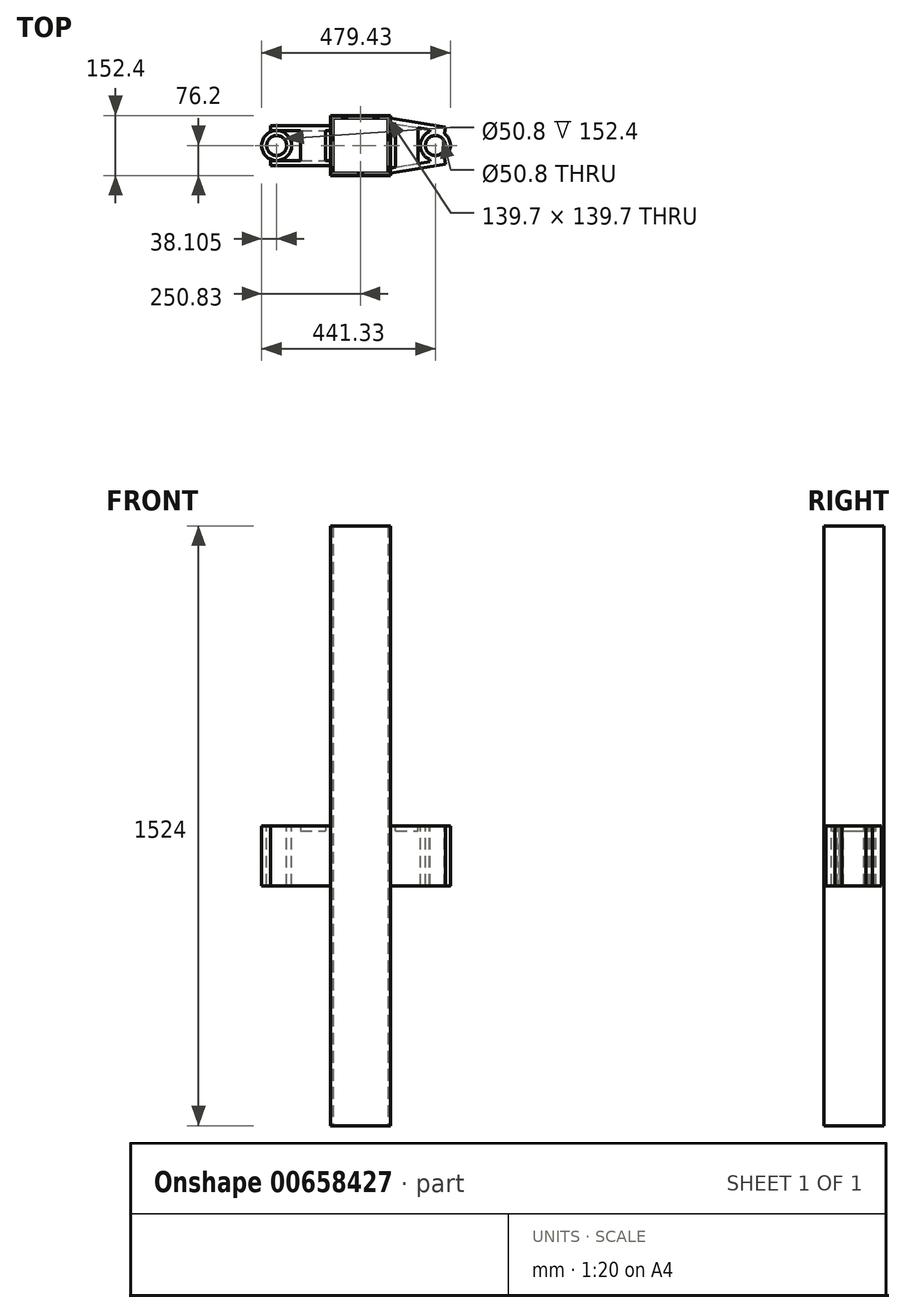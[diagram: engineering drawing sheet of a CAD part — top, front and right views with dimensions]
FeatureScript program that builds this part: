
annotation { "Feature Type Name" : "Feature", "Feature Type Description" : "" }
export const myFeature = defineFeature(function(context is Context, id is Id, definition is map)
    precondition{}
    {
        {
            var Q0;
            Q0=qCreatedBy(makeId("Top.planeOp"),FACE);
            var sketch = newSketch(context, id + "F0", { "sketchPlane" : qUnion([Q0])});
            skLineSegment(sketch, "E0.bottom", {"start": v(-76.2, -76.2) * mm, "end": v(76.2, -76.2) * mm});
            skLineSegment(sketch, "E0.top", {"start": v(-76.2, 76.2) * mm, "end": v(76.2, 76.2) * mm});
            skLineSegment(sketch, "E0.left", {"start": v(-76.2, -76.2) * mm, "end": v(-76.2, 76.2) * mm});
            skLineSegment(sketch, "E0.right", {"start": v(76.2, -76.2) * mm, "end": v(76.2, 76.2) * mm});
            skLineSegment(sketch, "E1.0", {"start": v(-69.85, 69.85) * mm, "end": v(69.85, 69.85) * mm});
            skLineSegment(sketch, "E1.1", {"start": v(-69.85, -69.85) * mm, "end": v(-69.85, 69.85) * mm});
            skLineSegment(sketch, "E1.2", {"start": v(-69.85, -69.85) * mm, "end": v(69.85, -69.85) * mm});
            skLineSegment(sketch, "E1.3", {"start": v(69.85, -69.85) * mm, "end": v(69.85, 69.85) * mm});
            skSolve(sketch);
        }
        {
            var Q0;
            Q0=makeQuery(id+"F0.imprint","IMPRINT",FACE,{"disambiguationData":[TD([[makeQuery(id+"F0.imprint","IMPRINT",EDGE,{"derivedFrom":sQuery(id+"F0.wireOp",EDGE,"E0.bottom")}),1.0]])]});
            extrude(context, id + "F1", {"entities" : qUnion([Q0]), "depth" : 1524 * mm, "offsetDistance" : 25.4 * mm});
        }
        {
            var Q0;
            Q0=makeQuery(id+"F1.opExtrude","SWEPT_FACE",FACE,{"disambiguationData":[OSD([sQuery(id+"F0.wireOp",EDGE,"E0.left")])]});
            var sketch = newSketch(context, id + "F2", { "sketchPlane" : qUnion([Q0])});
            skLineSegment(sketch, "E2.bottom", {"start": v(-50.8, 609.6) * mm, "end": v(-38.1, 609.6) * mm});
            skLineSegment(sketch, "E2.top", {"start": v(-50.8, 762) * mm, "end": v(-38.1, 762) * mm});
            skLineSegment(sketch, "E2.left", {"start": v(-50.8, 609.6) * mm, "end": v(-50.8, 762) * mm});
            skLineSegment(sketch, "E2.right", {"start": v(-38.1, 609.6) * mm, "end": v(-38.1, 762) * mm});
            skLineSegment(sketch, "E3.bottom", {"start": v(38.1, 762) * mm, "end": v(50.8, 762) * mm});
            skLineSegment(sketch, "E3.top", {"start": v(38.1, 609.6) * mm, "end": v(50.8, 609.6) * mm});
            skLineSegment(sketch, "E3.left", {"start": v(38.1, 762) * mm, "end": v(38.1, 609.6) * mm});
            skLineSegment(sketch, "E3.right", {"start": v(50.8, 762) * mm, "end": v(50.8, 609.6) * mm});
            skSolve(sketch);
        }
        {
            var Q0;
            Q0=makeQuery(id+"F2.imprint","IMPRINT",FACE,{"disambiguationData":[TD([[makeQuery(id+"F2.imprint","IMPRINT",EDGE,{"derivedFrom":sQuery(id+"F2.wireOp",EDGE,"E2.bottom")}),1.0]])]});
            var Q1;
            Q1=makeQuery(id+"F2.imprint","IMPRINT",FACE,{"disambiguationData":[TD([[makeQuery(id+"F2.imprint","IMPRINT",EDGE,{"derivedFrom":sQuery(id+"F2.wireOp",EDGE,"E3.bottom")}),-1.0]])]});
            extrude(context, id + "F3", {"entities" : qUnion([Q0, Q1]), "operationType" : NewBodyOperationType.ADD, "depth" : 152.4 * mm, "offsetDistance" : 25.4 * mm});
        }
        {
            var Q0;
            Q0=makeQuery(id+"F3.opExtrude","SWEPT_FACE",FACE,{"disambiguationData":[OSD([sQuery(id+"F2.wireOp",EDGE,"E2.top")])]});
            var sketch = newSketch(context, id + "F4", { "sketchPlane" : qUnion([Q0])});
            skCircle(sketch, "E4", {"center": v(-212.72, 0) * mm, "radius": 38.1 * mm});
            skCircle(sketch, "E5.0", {"center": v(-212.72, 0) * mm, "radius": 25.4 * mm});
            skSolve(sketch);
        }
        {
            var Q0;
            Q0=makeQuery(id+"F4.imprint","IMPRINT",FACE,{"disambiguationData":[TD([[makeQuery(id+"F4.imprint","IMPRINT",EDGE,{"derivedFrom":sQuery(id+"F4.wireOp",EDGE,"E4")}),1.0]])]});
            extrude(context, id + "F5", {"entities" : qUnion([Q0]), "operationType" : NewBodyOperationType.ADD, "oppositeDirection" : true, "depth" : 152.4 * mm, "offsetDistance" : 25.4 * mm});
        }
        {
            var Q0;
            Q0=makeQuery(id+"F3.opExtrude","SWEPT_FACE",FACE,{"disambiguationData":[OSD([sQuery(id+"F2.wireOp",EDGE,"E2.right")])]});
            var sketch = newSketch(context, id + "F6", { "sketchPlane" : qUnion([Q0])});
            skLineSegment(sketch, "E6.bottom", {"start": v(-152.4, 762) * mm, "end": v(-88.9, 762) * mm});
            skLineSegment(sketch, "E6.top", {"start": v(-152.4, 749.3) * mm, "end": v(-88.9, 749.3) * mm});
            skLineSegment(sketch, "E6.left", {"start": v(-152.4, 762) * mm, "end": v(-152.4, 749.3) * mm});
            skLineSegment(sketch, "E6.right", {"start": v(-88.9, 762) * mm, "end": v(-88.9, 749.3) * mm});
            skSolve(sketch);
        }
        {
            var Q0;
            Q0=makeQuery(id+"F6.imprint","IMPRINT",FACE,{"disambiguationData":[TD([[makeQuery(id+"F6.imprint","IMPRINT",EDGE,{"derivedFrom":sQuery(id+"F6.wireOp",EDGE,"E6.bottom")}),-1.0]])]});
            extrude(context, id + "F7", {"entities" : qUnion([Q0]), "operationType" : NewBodyOperationType.ADD, "endBound" : BoundingType.UP_TO_NEXT, "depth" : 25.4 * mm, "offsetDistance" : 25.4 * mm});
        }
        {
            var Q0;
            Q0=makeQuery(id+"F7.boolean.opBoolean","MERGE",FACE,{"derivedFrom":[makeQuery(id+"F3.opExtrude","SWEPT_FACE",FACE,{"disambiguationData":[OSD([sQuery(id+"F2.wireOp",EDGE,"E2.top")])]}),makeQuery(id+"F3.opExtrude","SWEPT_FACE",FACE,{"disambiguationData":[OSD([sQuery(id+"F2.wireOp",EDGE,"E3.bottom")])]}),makeQuery(id+"F7.opExtrude","SWEPT_FACE",FACE,{"disambiguationData":[OSD([sQuery(id+"F6.wireOp",EDGE,"E6.bottom")])]})]});
            var sketch = newSketch(context, id + "F8", { "sketchPlane" : qUnion([Q0])});
            skLineSegment(sketch, "E7.0", {"start": v(76.2, -76.2) * mm, "end": v(76.2, 76.2) * mm});
            skLineSegment(sketch, "E8.bottom", {"start": v(76.2, -76.2) * mm, "end": v(228.6, -76.2) * mm});
            skLineSegment(sketch, "E8.top", {"start": v(76.2, 76.2) * mm, "end": v(228.6, 76.2) * mm});
            skLineSegment(sketch, "E8.right", {"start": v(228.6, -76.2) * mm, "end": v(228.6, 76.2) * mm});
            skPoint(sketch, "E9", {"position": v(-228.6, 50.8) * mm});
            skPoint(sketch, "E10", {"position": v(-76.2, 50.8) * mm});
            skPoint(sketch, "E11", {"position": v(-228.6, 38.1) * mm});
            skPoint(sketch, "E12", {"position": v(-228.6, -38.1) * mm});
            skCircle(sketch, "E13", {"center": v(190.5, 0) * mm, "radius": 38.1 * mm});
            skPoint(sketch, "E13.centerSnap0", {"position": v(228.6, 0) * mm});
            skCircle(sketch, "E14", {"center": v(190.5, 0) * mm, "radius": 25.4 * mm});
            skLineSegment(sketch, "E15", {"start": v(76.2, 57.05) * mm, "end": v(214.11, 34.78) * mm});
            skLineSegment(sketch, "E16", {"start": v(76.2, -57.05) * mm, "end": v(214.11, -34.78) * mm});
            skLineSegment(sketch, "E17.0", {"start": v(76.2, 69.92) * mm, "end": v(216.14, 47.32) * mm});
            skLineSegment(sketch, "E18.0", {"start": v(76.2, -69.92) * mm, "end": v(216.14, -47.32) * mm});
            skLineSegment(sketch, "E19", {"start": v(216.14, 47.32) * mm, "end": v(213.41, 30.44) * mm});
            skLineSegment(sketch, "E20", {"start": v(216.14, -47.32) * mm, "end": v(213.41, -30.44) * mm});
            skLineSegment(sketch, "E21", {"start": v(176.5, -40.85) * mm, "end": v(175.56, -35.05) * mm});
            skLineSegment(sketch, "E22", {"start": v(176.5, 40.85) * mm, "end": v(175.56, 35.05) * mm});
            skSolve(sketch);
        }
        {
            var Q0;
            {var subQ7=sQuery(id+"F8.wireOp",EDGE,"E17.0");Q0=makeQuery(id+"F8.imprint","IMPRINT",FACE,{"disambiguationData":[TD([[makeQuery(id+"F8.imprint","IMPRINT",EDGE,{"derivedFrom":subQ7}),-1.0]])]});}
            var Q1;
            {var subQ0=sQuery(id+"F8.wireOp",EDGE,"E22");Q1=makeQuery(id+"F8.imprint","IMPRINT",FACE,{"disambiguationData":[TD([[makeQuery(id+"F8.imprint","IMPRINT",EDGE,{"derivedFrom":subQ0}),1.0]])]});}
            var Q2;
            {var subQ0=sQuery(id+"F8.wireOp",EDGE,"E19");var subQ1=sQuery(id+"F8.wireOp",EDGE,"E13");var subQ2=makeQuery(id+"F8.imprint","INTERSECT",VERTEX,{"derivedFrom":[subQ1,subQ0]});Q2=makeQuery(id+"F8.imprint","IMPRINT",FACE,{"disambiguationData":[TD([[makeQuery(id+"F8.imprint","IMPRINT",EDGE,{"disambiguationData":[TD([[subQ2,-1.0]])],"derivedFrom":subQ1}),-1.0]])]});}
            var Q3;
            Q3=makeQuery(id+"F8.imprint","IMPRINT",FACE,{"disambiguationData":[TD([[makeQuery(id+"F8.imprint","IMPRINT",EDGE,{"derivedFrom":sQuery(id+"F8.wireOp",EDGE,"E14")}),-1.0]])]});
            var Q4;
            {var subQ0=sQuery(id+"F8.wireOp",EDGE,"E20");var subQ1=sQuery(id+"F8.wireOp",EDGE,"E13");var subQ2=makeQuery(id+"F8.imprint","INTERSECT",VERTEX,{"derivedFrom":[subQ1,subQ0]});Q4=makeQuery(id+"F8.imprint","IMPRINT",FACE,{"disambiguationData":[TD([[makeQuery(id+"F8.imprint","IMPRINT",EDGE,{"disambiguationData":[TD([[subQ2,1.0]])],"derivedFrom":subQ1}),-1.0]])]});}
            var Q5;
            {var subQ0=sQuery(id+"F8.wireOp",EDGE,"E21");Q5=makeQuery(id+"F8.imprint","IMPRINT",FACE,{"disambiguationData":[TD([[makeQuery(id+"F8.imprint","IMPRINT",EDGE,{"derivedFrom":subQ0}),-1.0]])]});}
            var Q6;
            {var subQ7=sQuery(id+"F8.wireOp",EDGE,"E18.0");Q6=makeQuery(id+"F8.imprint","IMPRINT",FACE,{"disambiguationData":[TD([[makeQuery(id+"F8.imprint","IMPRINT",EDGE,{"derivedFrom":subQ7}),1.0]])]});}
            extrude(context, id + "F9", {"entities" : qUnion([Q0, Q1, Q2, Q3, Q4, Q5, Q6]), "operationType" : NewBodyOperationType.ADD, "oppositeDirection" : true, "depth" : 152.4 * mm, "offsetDistance" : 25.4 * mm});
        }
        {
            var Q0;
            Q0=makeQuery(id+"F9.opExtrude","CAP_FACE",FACE,{"disambiguationData":[OSD([sQuery(id+"F8.wireOp",EDGE,"E7.0"),sQuery(id+"F8.wireOp",EDGE,"E13"),sQuery(id+"F8.wireOp",EDGE,"E14"),sQuery(id+"F8.wireOp",EDGE,"E15"),sQuery(id+"F8.wireOp",EDGE,"E16"),sQuery(id+"F8.wireOp",EDGE,"E17.0"),sQuery(id+"F8.wireOp",EDGE,"E18.0"),sQuery(id+"F8.wireOp",EDGE,"E19"),sQuery(id+"F8.wireOp",EDGE,"E20"),sQuery(id+"F8.wireOp",EDGE,"E21"),sQuery(id+"F8.wireOp",EDGE,"E22")])],"isStart":true});
            var sketch = newSketch(context, id + "F10", { "sketchPlane" : qUnion([Q0])});
            skLineSegment(sketch, "E23", {"start": v(88.9, -55) * mm, "end": v(88.9, 55) * mm});
            skLineSegment(sketch, "E24", {"start": v(146.05, -45.77) * mm, "end": v(146.05, 45.77) * mm});
            skSolve(sketch);
        }
        {
            var Q0;
            {var subQ0=sQuery(id+"F10.wireOp",EDGE,"E23");Q0=makeQuery(id+"F10.imprint","IMPRINT",FACE,{"disambiguationData":[TD([[makeQuery(id+"F10.imprint","IMPRINT",EDGE,{"derivedFrom":subQ0}),-1.0]])]});}
            extrude(context, id + "F11", {"entities" : qUnion([Q0]), "operationType" : NewBodyOperationType.ADD, "oppositeDirection" : true, "depth" : 12.7 * mm, "offsetDistance" : 25.4 * mm});
        }
    });
